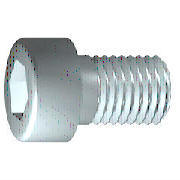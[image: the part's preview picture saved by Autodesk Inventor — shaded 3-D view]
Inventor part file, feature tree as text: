
AUTODESK INVENTOR PART (.ipt)
format: ipt  version: 2020 (Build 240168000, 168)  size: 202,240 bytes
history: native  units: mm (DEFAULTED — no unit token found)
features: sketch x2, other x1, extrude x1, plane x1, fillet x1
ambient origin geometry x7: Origin, YZ Plane, XY Plane, X Axis, Y Axis, Z Axis, Center Point
bodies: Solid1 (feature_tree)
feature tree (6):
  other  "Bryła"
  extrude  "Szczelina"  Depth=5.6mm
  plane  "Work Plane1"
  fillet  "Fillet2"  Radius=0.49086mm
  sketch  "Szkic1"
  sketch  "Szkic2"
